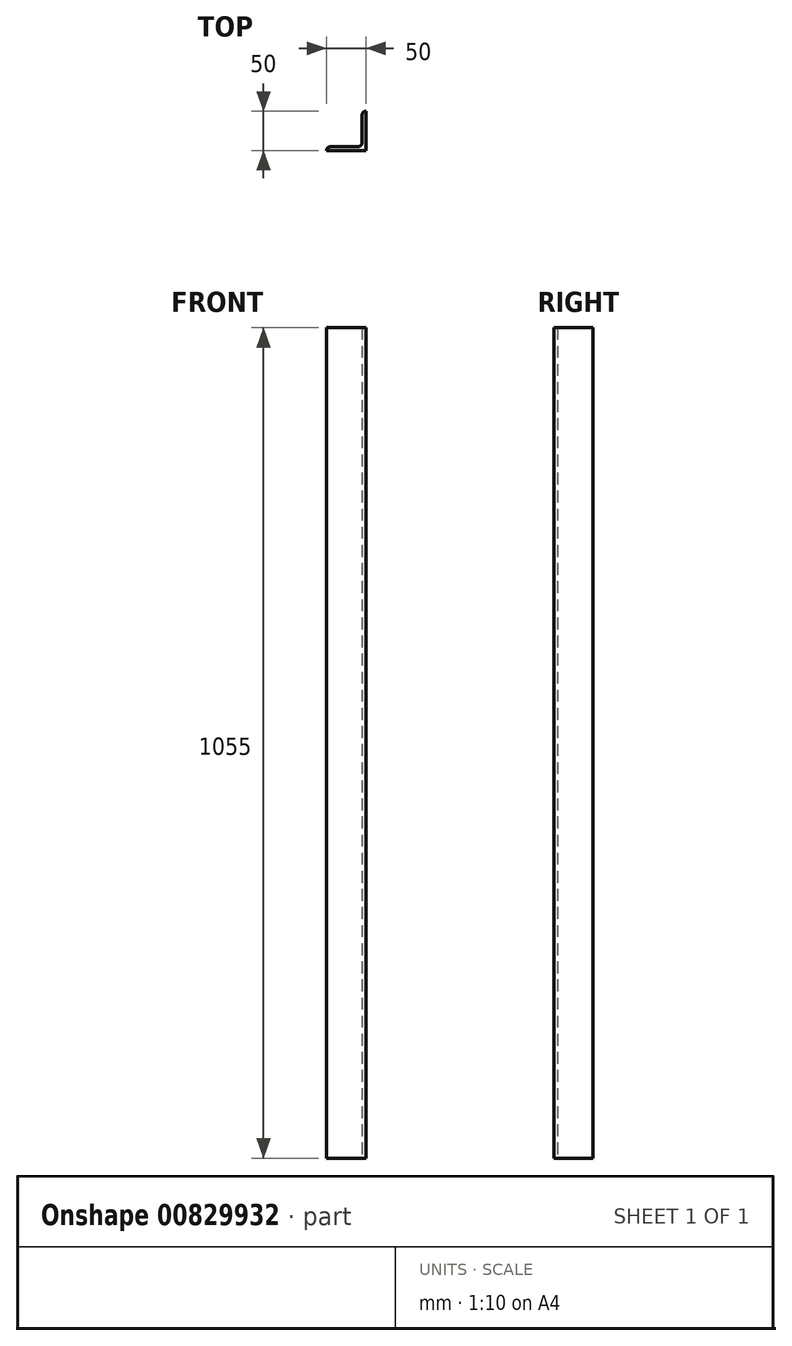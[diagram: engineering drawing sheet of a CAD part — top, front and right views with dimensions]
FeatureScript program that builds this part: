
annotation { "Feature Type Name" : "Feature", "Feature Type Description" : "" }
export const myFeature = defineFeature(function(context is Context, id is Id, definition is map)
    precondition{}
    {
        {
            var Q0;
            Q0=qCreatedBy(makeId("Top.planeOp"),FACE);
            var sketch = newSketch(context, id + "F0", { "sketchPlane" : qUnion([Q0])});
            skLineSegment(sketch, "E0", {"start": v(0, 0) * mm, "end": v(0, 50) * mm});
            skLineSegment(sketch, "E1", {"start": v(0, 0) * mm, "end": v(-50, 0) * mm});
            skLineSegment(sketch, "E2", {"start": v(-50, 0) * mm, "end": v(-50, 0) * mm});
            skLineSegment(sketch, "E3", {"start": v(-45, 5) * mm, "end": v(-10, 5) * mm});
            skLineSegment(sketch, "E4", {"start": v(-5, 10) * mm, "end": v(-5, 45) * mm});
            skLineSegment(sketch, "E5", {"start": v(0, 50) * mm, "end": v(0, 50) * mm});
            skPoint(sketch, "E6.visualSharp", {"position": v(-50, 5) * mm});
            skArc(sketch, "E6.filletArc", {"start": v(-45, 5) * mm, "mid": v(-48.54, 3.54) * mm, "end": v(-50, 0) * mm});
            skPoint(sketch, "E7.visualSharp", {"position": v(-5, 50) * mm});
            skArc(sketch, "E7.filletArc", {"start": v(0, 50) * mm, "mid": v(-3.54, 48.54) * mm, "end": v(-5, 45) * mm});
            skPoint(sketch, "E8.visualSharp", {"position": v(-5, 5) * mm});
            skArc(sketch, "E8.filletArc", {"start": v(-10, 5) * mm, "mid": v(-6.46, 6.46) * mm, "end": v(-5, 10) * mm});
            skSolve(sketch);
        }
        {
            var Q0;
            Q0=makeQuery(id+"F0.imprint","IMPRINT",FACE,{"disambiguationData":[TD([[makeQuery(id+"F0.imprint","IMPRINT",EDGE,{"derivedFrom":sQuery(id+"F0.wireOp",EDGE,"E0")}),1.0]])]});
            extrude(context, id + "F1", {"entities" : qUnion([Q0]), "depth" : 1055 * mm, "offsetDistance" : 25 * mm});
        }
    });
